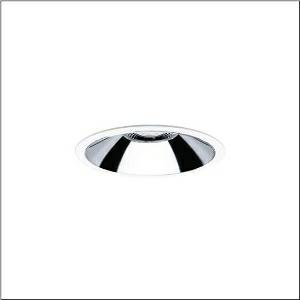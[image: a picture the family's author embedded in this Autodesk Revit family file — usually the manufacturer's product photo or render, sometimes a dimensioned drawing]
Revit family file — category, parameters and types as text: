
# Revit family: lunis_21_xl_51db15df43
name_source: partatom
category: Lighting Fixtures
units: mm (PartAtom-declared; Revit-internal decimal feet)

## family parameters
Cut with Voids When Loaded = No
Host = Face
Light Source = No
Part Type = Normal
Room Calculation Point = No
Round Connector Dimension = Use Diameter
Shared = No

## types (1)
- Lunis 21 XL (1 x LED, 3560 lm, 31 W, 4000K)
    Apparent Load = 31 VA
    CIE Flux Codes = 89 99 100 100 100
    Color Rendering = 80
    Color Temperature = 4000K
    Default Elevation = 1800 mm
    Description = Lunis 21,  XL, downlight, of PC, light emission: direct distribution, LED rated luminous flux: 3.560lm, light colour: 840, control gear: ECG DALI, with terminal, 5-pole, mains connection: 220..240V, AC, housing, round, of diecast aluminium, traffic white (RAL 9016), diameter: 213mm, protection rating (complete): IP20, insulation class (complete): insulation class II (safety insulation), certification: CE, impact resistance: IK02, packaging unit: 1 piece
    Height = 0 mm  [stored 0 ft]
    Lamp = 1 x LED
    Lamp Light Flux = 3560 lm
    Lamp Power = 31 W
    Lamp count = 1
    Length = 213 mm
    Luminous efficacy = 115 lm/W
    Manufacturer = Siteco
    ModVariant = No
    Model = 51DB15DF43
    Mounting Place = Ceiling
    Mounting Type = Recessed
    Number of Poles = 1
    OnlyDefault = Yes
    Power Factor = 1
    Product Name = Lunis 21 XL
    Product group = downlight | ceiling recessed
    ProductGroupID = 402
    Protection Class = Protection class II
    Protection Degree = IP 20
    RLX_Detail_Level = 1
    RlxData = <blob elided: 26981 chars, md5=a85729f8>
    Socket = socket
    Standby Power = 0 W
    System Light Flux = 3560 lm
    System Power = 31 W
    Type Comments = Product without accessories
    Type Image = l_1006990.jpg
    URL = http://relux.com
    VarID = ---
    Voltage = 0 V
    Weight = 0.00 kg
    Width = 0 mm  [stored 0 ft]

note: [stored X ft] marks values corroborated as IEEE doubles in the binary element streams (Revit-internal decimal feet)

## geometry (parser evidence)
native form markers: Blend x4, Sweep x10
no freeform markers — native parametric forms only
